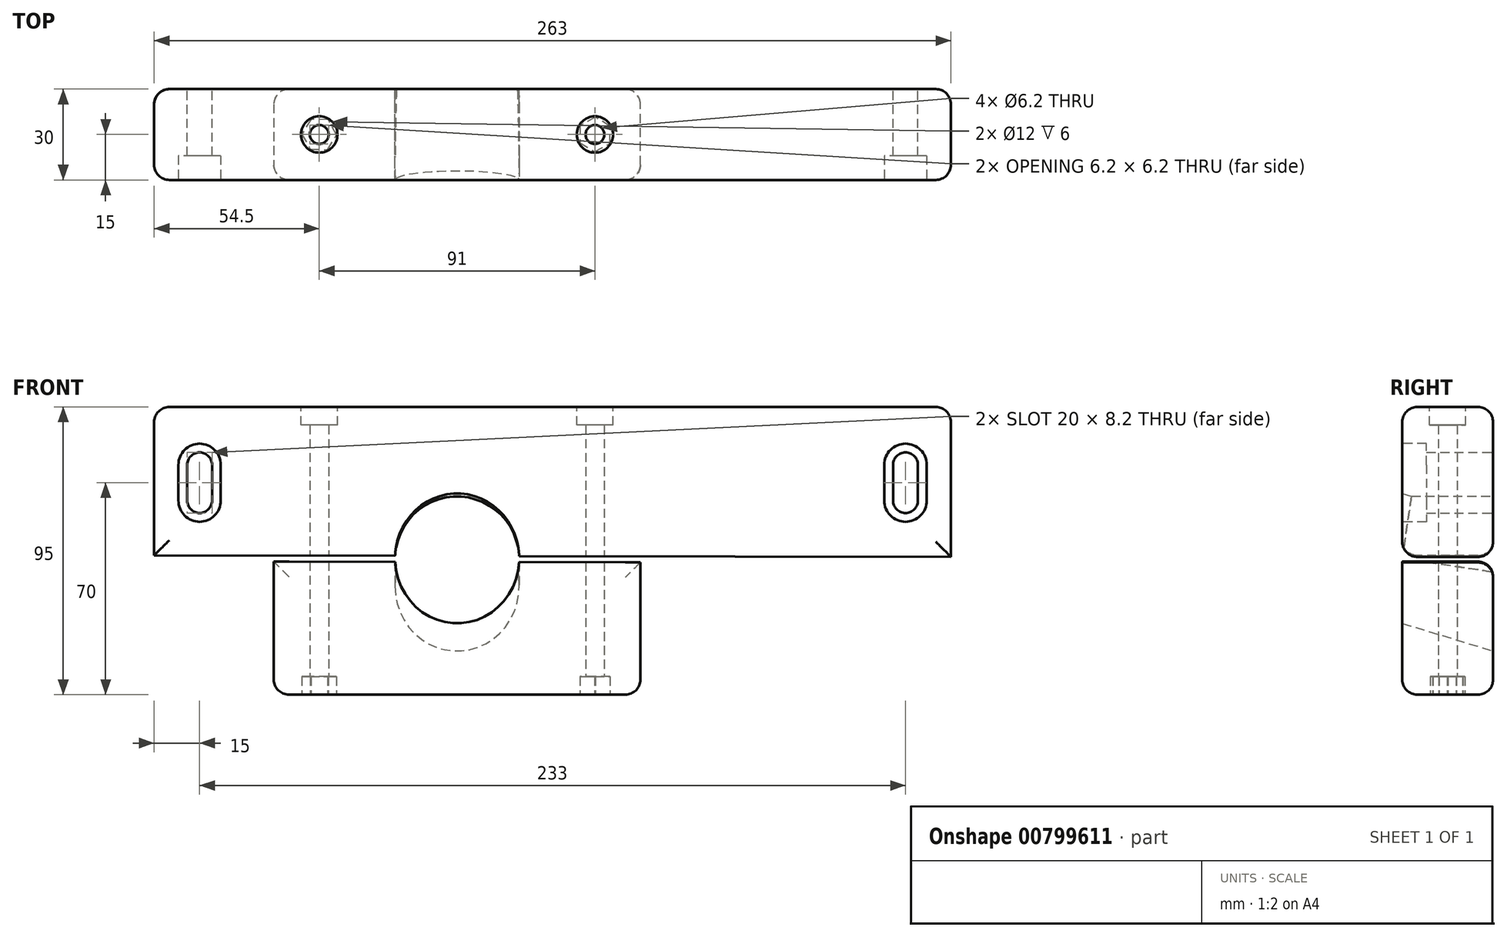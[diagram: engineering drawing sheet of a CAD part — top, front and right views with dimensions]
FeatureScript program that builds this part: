
annotation { "Feature Type Name" : "Feature", "Feature Type Description" : "" }
export const myFeature = defineFeature(function(context is Context, id is Id, definition is map)
    precondition{}
    {
        {
            var Q0;
            Q0=qCreatedBy(makeId("Front.planeOp"),FACE);
            var sketch = newSketch(context, id + "F0", { "sketchPlane" : qUnion([Q0])});
            skLineSegment(sketch, "E0", {"start": v(0, 0) * mm, "end": v(131.5, 0) * mm});
            skLineSegment(sketch, "E1", {"start": v(0, 0) * mm, "end": v(-131.5, 0) * mm});
            skLineSegment(sketch, "E2", {"start": v(-131.5, 0) * mm, "end": v(-131.5, -50) * mm});
            skLineSegment(sketch, "E3", {"start": v(131.5, 0) * mm, "end": v(131.5, -50) * mm});
            skLineSegment(sketch, "E4", {"start": v(131.5, -50) * mm, "end": v(-131.5, -50) * mm});
            skLineSegment(sketch, "E5.0", {"start": v(116.5, 0) * mm, "end": v(116.5, -19.1) * mm, "construction": true});
            skLineSegment(sketch, "E6.0", {"start": v(-116.5, 0) * mm, "end": v(-116.5, -19.1) * mm, "construction": true});
            skLineSegment(sketch, "E7.0", {"start": v(-112.4, 0) * mm, "end": v(-112.4, -50) * mm, "construction": true});
            skLineSegment(sketch, "E8.0", {"start": v(112.4, 0) * mm, "end": v(112.4, -50) * mm, "construction": true});
            skLineSegment(sketch, "E9.0", {"start": v(0, -19.1) * mm, "end": v(-131.5, -19.1) * mm, "construction": true});
            skLineSegment(sketch, "E10.0", {"start": v(131.5, -30.9) * mm, "end": v(-108.3, -30.9) * mm, "construction": true});
            skLineSegment(sketch, "E11.0", {"start": v(0, -19.1) * mm, "end": v(131.5, -19.1) * mm, "construction": true});
            skLineSegment(sketch, "E12.trimOffspring", {"start": v(-116.5, -30.9) * mm, "end": v(-131.5, -30.9) * mm, "construction": true});
            skArc(sketch, "E13", {"start": v(120.6, -19.1) * mm, "mid": v(116.5, -15) * mm, "end": v(112.4, -19.1) * mm});
            skArc(sketch, "E14", {"start": v(112.4, -30.9) * mm, "mid": v(116.5, -35) * mm, "end": v(120.6, -30.9) * mm});
            skArc(sketch, "E15", {"start": v(-120.6, -30.9) * mm, "mid": v(-116.5, -35) * mm, "end": v(-112.4, -30.9) * mm});
            skArc(sketch, "E16", {"start": v(-112.4, -19.1) * mm, "mid": v(-116.5, -15) * mm, "end": v(-120.6, -19.1) * mm});
            skLineSegment(sketch, "E17", {"start": v(-116.5, -25) * mm, "end": v(-31.5, -25) * mm, "construction": true});
            skLineSegment(sketch, "E18", {"start": v(-31.5, -25) * mm, "end": v(116.5, -25) * mm, "construction": true});
            skLineSegment(sketch, "E19.trimOffspring", {"start": v(116.5, -23.2) * mm, "end": v(116.5, -50) * mm, "construction": true});
            skLineSegment(sketch, "E20", {"start": v(120.6, -19.1) * mm, "end": v(120.6, -30.9) * mm});
            skLineSegment(sketch, "E21", {"start": v(112.4, -30.9) * mm, "end": v(112.4, -19.1) * mm});
            skLineSegment(sketch, "E22", {"start": v(-120.6, -19.1) * mm, "end": v(-120.6, -30.9) * mm});
            skLineSegment(sketch, "E23", {"start": v(-112.4, -19.1) * mm, "end": v(-112.4, -30.9) * mm});
            skLineSegment(sketch, "E24.trimOffspring", {"start": v(-116.5, -23.2) * mm, "end": v(-116.5, -50) * mm, "construction": true});
            skLineSegment(sketch, "E25", {"start": v(-31.5, -25) * mm, "end": v(-31.5, -50) * mm, "construction": true});
            skCircle(sketch, "E26", {"center": v(-31.5, -50) * mm, "radius": 20.5 * mm});
            skLineSegment(sketch, "E27", {"start": v(-52, -50) * mm, "end": v(-92, -50) * mm, "construction": true});
            skLineSegment(sketch, "E28", {"start": v(-92, -50) * mm, "end": v(-92, -95) * mm});
            skLineSegment(sketch, "E29", {"start": v(-92, -95) * mm, "end": v(29, -95) * mm});
            skLineSegment(sketch, "E30", {"start": v(29, -95) * mm, "end": v(29, -50) * mm});
            skSolve(sketch);
        }
        {
            var Q0;
            Q0=makeQuery(id+"F0.imprint","IMPRINT",FACE,{"disambiguationData":[TD([[makeQuery(id+"F0.imprint","IMPRINT",EDGE,{"derivedFrom":sQuery(id+"F0.wireOp",EDGE,"E0")}),-1.0]])]});
            var Q1;
            {var subQ0=sQuery(id+"F0.wireOp",EDGE,"E28");Q1=makeQuery(id+"F0.imprint","IMPRINT",FACE,{"disambiguationData":[TD([[makeQuery(id+"F0.imprint","IMPRINT",EDGE,{"derivedFrom":subQ0}),1.0]])]});}
            var Q2;
            {var subQ0=sQuery(id+"F0.wireOp",EDGE,"E26");var subQ1=sQuery(id+"F0.wireOp",EDGE,"E4");var subQ2=makeQuery(id+"F0.imprint","INTERSECT",VERTEX,{"disambiguationData":[OD(0.0)],"derivedFrom":[subQ1,subQ0]});Q2=makeQuery(id+"F0.imprint","IMPRINT",FACE,{"disambiguationData":[TD([[makeQuery(id+"F0.imprint","IMPRINT",EDGE,{"disambiguationData":[TD([[subQ2,-1.0]])],"derivedFrom":subQ1}),1.0]])]});}
            var Q3;
            {var subQ0=sQuery(id+"F0.wireOp",EDGE,"E26");var subQ1=sQuery(id+"F0.wireOp",EDGE,"E4");var subQ2=makeQuery(id+"F0.imprint","INTERSECT",VERTEX,{"disambiguationData":[OD(0.0)],"derivedFrom":[subQ1,subQ0]});Q3=makeQuery(id+"F0.imprint","IMPRINT",FACE,{"disambiguationData":[TD([[makeQuery(id+"F0.imprint","IMPRINT",EDGE,{"disambiguationData":[TD([[subQ2,-1.0]])],"derivedFrom":subQ1}),-1.0]])]});}
            extrude(context, id + "F1", {"entities" : qUnion([Q0, Q1, Q2, Q3]), "depth" : 30 * mm, "offsetDistance" : 25 * mm});
        }
        {
            var Q0;
            Q0=qCreatedBy(makeId("Front.planeOp"),FACE);
            var Q1;
            {var subQ0=sQuery(id+"F0.wireOp",EDGE,"E4");Q1=makeQuery(id+"F1.opExtrude","CAP_EDGE",EDGE,{"disambiguationData":[OSD([subQ0]),TDD([makeQuery(id+"F0.imprint","IMPRINT",EDGE,{"disambiguationData":[TD([[makeQuery(id+"F0.imprint","INTERSECT",VERTEX,{"derivedFrom":[sQuery(id+"F0.wireOp",EDGE,"E2"),subQ0]}),1.0]])],"derivedFrom":subQ0})])],"isStart":false});}
            cPlane(context, id + "F2", {"entities" : qUnion([Q0, Q1]), "cplaneType" : CPlaneType.LINE_ANGLE, "offset" : 25 * mm, "angle" : 17 * degree, "width" : 150 * mm, "height" : 150 * mm});
        }
        {
            var Q0;
            Q0=qCreatedBy(id+"F2.planeOp",FACE);
            var sketch = newSketch(context, id + "F3", { "sketchPlane" : qUnion([Q0])});
            skPoint(sketch, "E31", {"position": v(92, -56.59) * mm});
            skPoint(sketch, "E32", {"position": v(112.4, -56.59) * mm});
            skLineSegment(sketch, "E33", {"start": v(92, -56.59) * mm, "end": v(31.5, -56.59) * mm, "construction": true});
            skCircle(sketch, "E34", {"center": v(31.5, -56.59) * mm, "radius": 20.5 * mm});
            skSolve(sketch);
        }
        {
            var Q0;
            Q0=makeQuery(id+"F3.imprint","IMPRINT",FACE,{"disambiguationData":[TD([[makeQuery(id+"F3.imprint","IMPRINT",EDGE,{"derivedFrom":sQuery(id+"F3.wireOp",EDGE,"E34")}),1.0]])]});
            extrude(context, id + "F4", {"entities" : qUnion([Q0]), "operationType" : NewBodyOperationType.REMOVE, "endBound" : BoundingType.SYMMETRIC, "oppositeDirection" : true, "depth" : 80 * mm, "offsetDistance" : 25 * mm});
        }
        {
            var Q0;
            Q0=makeQuery(id+"F1.opExtrude","CAP_FACE",FACE,{"disambiguationData":[OSD([sQuery(id+"F0.wireOp",EDGE,"E0"),sQuery(id+"F0.wireOp",EDGE,"E1"),sQuery(id+"F0.wireOp",EDGE,"E2"),sQuery(id+"F0.wireOp",EDGE,"E3"),sQuery(id+"F0.wireOp",EDGE,"E4"),sQuery(id+"F0.wireOp",EDGE,"E13"),sQuery(id+"F0.wireOp",EDGE,"E14"),sQuery(id+"F0.wireOp",EDGE,"E15"),sQuery(id+"F0.wireOp",EDGE,"E16"),sQuery(id+"F0.wireOp",EDGE,"E20"),sQuery(id+"F0.wireOp",EDGE,"E21"),sQuery(id+"F0.wireOp",EDGE,"E22"),sQuery(id+"F0.wireOp",EDGE,"E23"),sQuery(id+"F0.wireOp",EDGE,"E28"),sQuery(id+"F0.wireOp",EDGE,"E29"),sQuery(id+"F0.wireOp",EDGE,"E30")])],"isStart":false});
            var sketch = newSketch(context, id + "F5", { "sketchPlane" : qUnion([Q0])});
            skLineSegment(sketch, "E35", {"start": v(-112.4, -19.1) * mm, "end": v(-120.6, -19.1) * mm, "construction": true});
            skLineSegment(sketch, "E36", {"start": v(-120.6, -19.1) * mm, "end": v(-120.6, -30.9) * mm, "construction": true});
            skArc(sketch, "E37", {"start": v(-109.5, -19.1) * mm, "mid": v(-116.5, -12.1) * mm, "end": v(-123.5, -19.1) * mm});
            skLineSegment(sketch, "E38", {"start": v(-123.5, -19.1) * mm, "end": v(-123.5, -30.9) * mm});
            skLineSegment(sketch, "E39", {"start": v(-109.5, -30.9) * mm, "end": v(-109.5, -19.1) * mm});
            skArc(sketch, "E40.trimOffspring", {"start": v(-123.5, -30.9) * mm, "mid": v(-116.5, -37.9) * mm, "end": v(-109.5, -30.9) * mm});
            skPoint(sketch, "E41.end.orphan", {"position": v(-112.4, -30.9) * mm});
            skLineSegment(sketch, "E42.MirrorCS", {"start": v(109.5, -30.9) * mm, "end": v(109.5, -19.1) * mm});
            skLineSegment(sketch, "E43.MirrorCS", {"start": v(123.5, -19.1) * mm, "end": v(123.5, -30.9) * mm});
            skArc(sketch, "E44.MirrorCS", {"start": v(109.5, -19.1) * mm, "mid": v(116.5, -12.1) * mm, "end": v(123.5, -19.1) * mm});
            skArc(sketch, "E45.MirrorCS", {"start": v(123.5, -30.9) * mm, "mid": v(116.5, -37.9) * mm, "end": v(109.5, -30.9) * mm});
            skSolve(sketch);
        }
        {
            var Q0;
            Q0=makeQuery(id+"F5.imprint","IMPRINT",FACE,{"disambiguationData":[TD([[makeQuery(id+"F5.imprint","IMPRINT",EDGE,{"derivedFrom":sQuery(id+"F5.wireOp",EDGE,"E37")}),1.0]])]});
            var Q1;
            Q1=makeQuery(id+"F5.imprint","IMPRINT",FACE,{"disambiguationData":[TD([[makeQuery(id+"F5.imprint","IMPRINT",EDGE,{"derivedFrom":sQuery(id+"F5.wireOp",EDGE,"E42.MirrorCS")}),-1.0]])]});
            extrude(context, id + "F6", {"entities" : qUnion([Q0, Q1]), "operationType" : NewBodyOperationType.REMOVE, "oppositeDirection" : true, "depth" : 8 * mm, "offsetDistance" : 25 * mm});
        }
        {
            var Q0;
            Q0=makeQuery(id+"F1.opExtrude","SWEPT_FACE",FACE,{"disambiguationData":[OSD([sQuery(id+"F0.wireOp",EDGE,"E29")])]});
            var sketch = newSketch(context, id + "F7", { "sketchPlane" : qUnion([Q0])});
            skLineSegment(sketch, "E46", {"start": v(-92, 30) * mm, "end": v(-92, 0) * mm, "construction": true});
            skLineSegment(sketch, "E47", {"start": v(-92, 0) * mm, "end": v(29, 0) * mm, "construction": true});
            skLineSegment(sketch, "E48", {"start": v(29, 0) * mm, "end": v(29, 15) * mm, "construction": true});
            skLineSegment(sketch, "E49", {"start": v(29, 15) * mm, "end": v(-92, 15) * mm, "construction": true});
            skLineSegment(sketch, "E50", {"start": v(-92, 15) * mm, "end": v(-77, 15) * mm, "construction": true});
            skLineSegment(sketch, "E51", {"start": v(-77, 15) * mm, "end": v(14, 15) * mm, "construction": true});
            skCircle(sketch, "E52", {"center": v(-77, 15) * mm, "radius": 3.1 * mm});
            skCircle(sketch, "E53", {"center": v(14, 15) * mm, "radius": 3.1 * mm});
            skCircle(sketch, "E54.cCircle", {"center": v(-77, 15) * mm, "radius": 4.95 * mm, "construction": true});
            skLineSegment(sketch, "E54.0", {"start": v(-74.24, 20) * mm, "end": v(-71.29, 15.1) * mm});
            skLineSegment(sketch, "E54.1", {"start": v(-71.29, 15.1) * mm, "end": v(-74.05, 10.1) * mm});
            skLineSegment(sketch, "E54.2", {"start": v(-74.05, 10.1) * mm, "end": v(-79.76, 10) * mm});
            skLineSegment(sketch, "E54.3", {"start": v(-79.76, 10) * mm, "end": v(-82.71, 14.9) * mm});
            skLineSegment(sketch, "E54.4", {"start": v(-82.71, 14.9) * mm, "end": v(-79.95, 19.9) * mm});
            skLineSegment(sketch, "E54.5", {"start": v(-79.95, 19.9) * mm, "end": v(-74.24, 20) * mm});
            skPoint(sketch, "E54.0.midPoint", {"position": v(-72.76, 17.56) * mm});
            skCircle(sketch, "E55.cCircle", {"center": v(14, 15) * mm, "radius": 4.95 * mm, "construction": true});
            skLineSegment(sketch, "E55.0", {"start": v(9, 17.76) * mm, "end": v(13.9, 20.71) * mm});
            skLineSegment(sketch, "E55.1", {"start": v(13.9, 20.71) * mm, "end": v(18.9, 17.95) * mm});
            skLineSegment(sketch, "E55.2", {"start": v(18.9, 17.95) * mm, "end": v(19, 12.24) * mm});
            skLineSegment(sketch, "E55.3", {"start": v(19, 12.24) * mm, "end": v(14.1, 9.29) * mm});
            skLineSegment(sketch, "E55.4", {"start": v(14.1, 9.29) * mm, "end": v(9.1, 12.05) * mm});
            skLineSegment(sketch, "E55.5", {"start": v(9.1, 12.05) * mm, "end": v(9, 17.76) * mm});
            skPoint(sketch, "E55.0.midPoint", {"position": v(11.44, 19.24) * mm});
            skSolve(sketch);
        }
        {
            var Q0;
            Q0=makeQuery(id+"F7.imprint","IMPRINT",FACE,{"disambiguationData":[TD([[makeQuery(id+"F7.imprint","IMPRINT",EDGE,{"derivedFrom":sQuery(id+"F7.wireOp",EDGE,"E52")}),1.0]])]});
            var Q1;
            Q1=makeQuery(id+"F7.imprint","IMPRINT",FACE,{"disambiguationData":[TD([[makeQuery(id+"F7.imprint","IMPRINT",EDGE,{"derivedFrom":sQuery(id+"F7.wireOp",EDGE,"E53")}),1.0]])]});
            extrude(context, id + "F8", {"entities" : qUnion([Q0, Q1]), "operationType" : NewBodyOperationType.REMOVE, "endBound" : BoundingType.UP_TO_NEXT, "oppositeDirection" : true, "depth" : 25 * mm, "offsetDistance" : 25 * mm});
        }
        {
            var Q0;
            Q0=makeQuery(id+"F7.imprint","IMPRINT",FACE,{"disambiguationData":[TD([[makeQuery(id+"F7.imprint","IMPRINT",EDGE,{"derivedFrom":sQuery(id+"F7.wireOp",EDGE,"E52")}),-1.0]])]});
            var Q1;
            Q1=makeQuery(id+"F7.imprint","IMPRINT",FACE,{"disambiguationData":[TD([[makeQuery(id+"F7.imprint","IMPRINT",EDGE,{"derivedFrom":sQuery(id+"F7.wireOp",EDGE,"E53")}),-1.0]])]});
            extrude(context, id + "F9", {"entities" : qUnion([Q0, Q1]), "operationType" : NewBodyOperationType.REMOVE, "oppositeDirection" : true, "depth" : 6 * mm, "offsetDistance" : 25 * mm});
        }
        {
            var Q0;
            Q0=makeQuery(id+"F1.opExtrude","SWEPT_FACE",FACE,{"disambiguationData":[OSD([sQuery(id+"F0.wireOp",EDGE,"E0"),sQuery(id+"F0.wireOp",EDGE,"E1")])]});
            var sketch = newSketch(context, id + "F10", { "sketchPlane" : qUnion([Q0])});
            skCircle(sketch, "E56", {"center": v(-77, -15) * mm, "radius": 6 * mm});
            skCircle(sketch, "E57", {"center": v(14, -15) * mm, "radius": 6 * mm});
            skSolve(sketch);
        }
        {
            var Q0;
            Q0 = qSketchRegion(id + "F10", true);
            extrude(context, id + "F11", {"entities" : qUnion([Q0]), "operationType" : NewBodyOperationType.REMOVE, "oppositeDirection" : true, "depth" : 6 * mm, "offsetDistance" : 25 * mm});
        }
        {
            var Q0;
            Q0=makeQuery(id+"F1.opExtrude","CAP_FACE",FACE,{"disambiguationData":[OSD([sQuery(id+"F0.wireOp",EDGE,"E0"),sQuery(id+"F0.wireOp",EDGE,"E1"),sQuery(id+"F0.wireOp",EDGE,"E2"),sQuery(id+"F0.wireOp",EDGE,"E3"),sQuery(id+"F0.wireOp",EDGE,"E4"),sQuery(id+"F0.wireOp",EDGE,"E13"),sQuery(id+"F0.wireOp",EDGE,"E14"),sQuery(id+"F0.wireOp",EDGE,"E15"),sQuery(id+"F0.wireOp",EDGE,"E16"),sQuery(id+"F0.wireOp",EDGE,"E20"),sQuery(id+"F0.wireOp",EDGE,"E21"),sQuery(id+"F0.wireOp",EDGE,"E22"),sQuery(id+"F0.wireOp",EDGE,"E23"),sQuery(id+"F0.wireOp",EDGE,"E28"),sQuery(id+"F0.wireOp",EDGE,"E29"),sQuery(id+"F0.wireOp",EDGE,"E30")])],"isStart":false});
            var sketch = newSketch(context, id + "F12", { "sketchPlane" : qUnion([Q0])});
            skLineSegment(sketch, "E58", {"start": v(-131.5, -50) * mm, "end": v(-131.5, -49) * mm});
            skLineSegment(sketch, "E59", {"start": v(-131.5, -49) * mm, "end": v(131.5, -49.5) * mm});
            skPoint(sketch, "E59.endSnap0", {"position": v(-131.5, -49.5) * mm});
            skLineSegment(sketch, "E60", {"start": v(131.5, -49.5) * mm, "end": v(131.5, -51.5) * mm});
            skLineSegment(sketch, "E61", {"start": v(-131.5, -49) * mm, "end": v(-131.5, -51) * mm});
            skLineSegment(sketch, "E62", {"start": v(-131.5, -51) * mm, "end": v(131.5, -51.5) * mm});
            skSolve(sketch);
        }
        {
            var Q0;
            {var subQ4=sQuery(id+"F0.wireOp",EDGE,"E4");var subQ5=sQuery(id+"F0.wireOp",EDGE,"E2");var subQ8=makeQuery(id+"F1.opExtrude","CAP_EDGE",EDGE,{"disambiguationData":[OSD([subQ4]),TDD([makeQuery(id+"F0.imprint","IMPRINT",EDGE,{"disambiguationData":[TD([[makeQuery(id+"F0.imprint","INTERSECT",VERTEX,{"derivedFrom":[subQ5,subQ4]}),1.0]])],"derivedFrom":subQ4})])],"isStart":false});Q0=makeQuery(id+"F12.imprint","IMPRINT",FACE,{"disambiguationData":[TD([[makeQuery(id+"F12.imprint","IMPRINT",EDGE,{"derivedFrom":subQ8}),-1.0]])]});}
            var Q1;
            {var subQ0=sQuery(id+"F12.wireOp",EDGE,"E59");var subQ1=makeQuery(id+"F4.boolean.opBoolean","INTERSECT",EDGE,{"derivedFrom":[makeQuery(id+"F1.opExtrude","CAP_FACE",FACE,{"disambiguationData":[OSD([sQuery(id+"F0.wireOp",EDGE,"E0"),sQuery(id+"F0.wireOp",EDGE,"E1"),sQuery(id+"F0.wireOp",EDGE,"E2"),sQuery(id+"F0.wireOp",EDGE,"E3"),sQuery(id+"F0.wireOp",EDGE,"E4"),sQuery(id+"F0.wireOp",EDGE,"E13"),sQuery(id+"F0.wireOp",EDGE,"E14"),sQuery(id+"F0.wireOp",EDGE,"E15"),sQuery(id+"F0.wireOp",EDGE,"E16"),sQuery(id+"F0.wireOp",EDGE,"E20"),sQuery(id+"F0.wireOp",EDGE,"E21"),sQuery(id+"F0.wireOp",EDGE,"E22"),sQuery(id+"F0.wireOp",EDGE,"E23"),sQuery(id+"F0.wireOp",EDGE,"E28"),sQuery(id+"F0.wireOp",EDGE,"E29"),sQuery(id+"F0.wireOp",EDGE,"E30")])],"isStart":false}),makeQuery(id+"F4.opExtrude","SWEPT_FACE",FACE,{"disambiguationData":[OSD([sQuery(id+"F3.wireOp",EDGE,"E34")])]})]});var subQ2=makeQuery(id+"F12.imprint","INTERSECT",VERTEX,{"disambiguationData":[OD(0.0)],"derivedFrom":[subQ1,subQ0]});Q1=makeQuery(id+"F12.imprint","IMPRINT",FACE,{"disambiguationData":[TD([[makeQuery(id+"F12.imprint","IMPRINT",EDGE,{"disambiguationData":[TD([[subQ2,-1.0]])],"derivedFrom":subQ0}),-1.0]])]});}
            var Q2;
            {var subQ0=sQuery(id+"F0.wireOp",EDGE,"E4");var subQ1=sQuery(id+"F0.wireOp",EDGE,"E3");var subQ3=makeQuery(id+"F1.opExtrude","CAP_EDGE",EDGE,{"disambiguationData":[OSD([subQ0]),TDD([makeQuery(id+"F0.imprint","IMPRINT",EDGE,{"disambiguationData":[TD([[makeQuery(id+"F0.imprint","INTERSECT",VERTEX,{"derivedFrom":[subQ1,subQ0]}),-1.0]])],"derivedFrom":subQ0})])],"isStart":false});Q2=makeQuery(id+"F12.imprint","IMPRINT",FACE,{"disambiguationData":[TD([[makeQuery(id+"F12.imprint","IMPRINT",EDGE,{"derivedFrom":subQ3}),-1.0]])]});}
            extrude(context, id + "F13", {"entities" : qUnion([Q0, Q1, Q2]), "operationType" : NewBodyOperationType.REMOVE, "oppositeDirection" : true, "depth" : 50 * mm, "offsetDistance" : 25 * mm});
        }
        {
            var Q0;
            Q0=makeQuery(id+"F1.opExtrude","CAP_EDGE",EDGE,{"disambiguationData":[OSD([sQuery(id+"F0.wireOp",EDGE,"E0"),sQuery(id+"F0.wireOp",EDGE,"E1")])],"isStart":false});
            var Q1;
            Q1=makeQuery(id+"F1.opExtrude","CAP_EDGE",EDGE,{"disambiguationData":[OSD([sQuery(id+"F0.wireOp",EDGE,"E2")])],"isStart":false});
            var Q2;
            Q2=makeQuery(id+"F1.opExtrude","CAP_EDGE",EDGE,{"disambiguationData":[OSD([sQuery(id+"F0.wireOp",EDGE,"E3")])],"isStart":false});
            var Q3;
            {var subQ0=sQuery(id+"F0.wireOp",EDGE,"E3");var subQ1=sQuery(id+"F12.wireOp",EDGE,"E59");Q3=makeQuery(id+"F13.boolean.opBoolean","COPY",EDGE,{"disambiguationData":[TD([makeQuery(id+"F1.opExtrude","SWEPT_FACE",FACE,{"disambiguationData":[OSD([subQ0])]})])],"derivedFrom":makeQuery(id+"F13.opExtrude","CAP_EDGE",EDGE,{"disambiguationData":[OSD([subQ1])],"isStart":true})});}
            var Q4;
            {var subQ0=sQuery(id+"F0.wireOp",EDGE,"E2");var subQ1=sQuery(id+"F12.wireOp",EDGE,"E59");Q4=makeQuery(id+"F13.boolean.opBoolean","COPY",EDGE,{"disambiguationData":[TD([makeQuery(id+"F1.opExtrude","SWEPT_FACE",FACE,{"disambiguationData":[OSD([subQ0])]})])],"derivedFrom":makeQuery(id+"F13.opExtrude","CAP_EDGE",EDGE,{"disambiguationData":[OSD([subQ1])],"isStart":true})});}
            var Q5;
            Q5=makeQuery(id+"F1.opExtrude","CAP_EDGE",EDGE,{"disambiguationData":[OSD([sQuery(id+"F0.wireOp",EDGE,"E29")])],"isStart":false});
            var Q6;
            Q6=makeQuery(id+"F1.opExtrude","CAP_EDGE",EDGE,{"disambiguationData":[OSD([sQuery(id+"F0.wireOp",EDGE,"E28")])],"isStart":false});
            var Q7;
            {var subQ0=sQuery(id+"F0.wireOp",EDGE,"E28");var subQ1=sQuery(id+"F12.wireOp",EDGE,"E62");Q7=makeQuery(id+"F13.boolean.opBoolean","COPY",EDGE,{"disambiguationData":[TD([makeQuery(id+"F1.opExtrude","SWEPT_FACE",FACE,{"disambiguationData":[OSD([subQ0])]})])],"derivedFrom":makeQuery(id+"F13.opExtrude","CAP_EDGE",EDGE,{"disambiguationData":[OSD([subQ1])],"isStart":true})});}
            var Q8;
            {var subQ0=sQuery(id+"F0.wireOp",EDGE,"E30");var subQ1=sQuery(id+"F12.wireOp",EDGE,"E62");Q8=makeQuery(id+"F13.boolean.opBoolean","COPY",EDGE,{"disambiguationData":[TD([makeQuery(id+"F1.opExtrude","SWEPT_FACE",FACE,{"disambiguationData":[OSD([subQ0])]})])],"derivedFrom":makeQuery(id+"F13.opExtrude","CAP_EDGE",EDGE,{"disambiguationData":[OSD([subQ1])],"isStart":true})});}
            var Q9;
            Q9=makeQuery(id+"F1.opExtrude","CAP_EDGE",EDGE,{"disambiguationData":[OSD([sQuery(id+"F0.wireOp",EDGE,"E30")])],"isStart":false});
            var Q10;
            Q10=makeQuery(id+"F1.opExtrude","SWEPT_EDGE",EDGE,{"disambiguationData":[OSD([sQuery(id+"F0.wireOp",EDGE,"E29"),sQuery(id+"F0.wireOp",EDGE,"E30")])]});
            var Q11;
            Q11=makeQuery(id+"F1.opExtrude","CAP_EDGE",EDGE,{"disambiguationData":[OSD([sQuery(id+"F0.wireOp",EDGE,"E30")])],"isStart":true});
            var Q12;
            Q12=makeQuery(id+"F1.opExtrude","CAP_EDGE",EDGE,{"disambiguationData":[OSD([sQuery(id+"F0.wireOp",EDGE,"E29")])],"isStart":true});
            var Q13;
            Q13=makeQuery(id+"F13.boolean.opBoolean","INTERSECT",EDGE,{"disambiguationData":[OD(1.0)],"derivedFrom":[makeQuery(id+"F1.opExtrude","CAP_FACE",FACE,{"disambiguationData":[OSD([sQuery(id+"F0.wireOp",EDGE,"E0"),sQuery(id+"F0.wireOp",EDGE,"E1"),sQuery(id+"F0.wireOp",EDGE,"E2"),sQuery(id+"F0.wireOp",EDGE,"E3"),sQuery(id+"F0.wireOp",EDGE,"E4"),sQuery(id+"F0.wireOp",EDGE,"E13"),sQuery(id+"F0.wireOp",EDGE,"E14"),sQuery(id+"F0.wireOp",EDGE,"E15"),sQuery(id+"F0.wireOp",EDGE,"E16"),sQuery(id+"F0.wireOp",EDGE,"E20"),sQuery(id+"F0.wireOp",EDGE,"E21"),sQuery(id+"F0.wireOp",EDGE,"E22"),sQuery(id+"F0.wireOp",EDGE,"E23"),sQuery(id+"F0.wireOp",EDGE,"E28"),sQuery(id+"F0.wireOp",EDGE,"E29"),sQuery(id+"F0.wireOp",EDGE,"E30")])],"isStart":true}),makeQuery(id+"F13.opExtrude","SWEPT_FACE",FACE,{"disambiguationData":[OSD([sQuery(id+"F12.wireOp",EDGE,"E62")])]})]});
            var Q14;
            Q14=makeQuery(id+"F1.opExtrude","CAP_EDGE",EDGE,{"disambiguationData":[OSD([sQuery(id+"F0.wireOp",EDGE,"E28")])],"isStart":true});
            var Q15;
            Q15=makeQuery(id+"F13.boolean.opBoolean","INTERSECT",EDGE,{"disambiguationData":[OD(0.0)],"derivedFrom":[makeQuery(id+"F1.opExtrude","CAP_FACE",FACE,{"disambiguationData":[OSD([sQuery(id+"F0.wireOp",EDGE,"E0"),sQuery(id+"F0.wireOp",EDGE,"E1"),sQuery(id+"F0.wireOp",EDGE,"E2"),sQuery(id+"F0.wireOp",EDGE,"E3"),sQuery(id+"F0.wireOp",EDGE,"E4"),sQuery(id+"F0.wireOp",EDGE,"E13"),sQuery(id+"F0.wireOp",EDGE,"E14"),sQuery(id+"F0.wireOp",EDGE,"E15"),sQuery(id+"F0.wireOp",EDGE,"E16"),sQuery(id+"F0.wireOp",EDGE,"E20"),sQuery(id+"F0.wireOp",EDGE,"E21"),sQuery(id+"F0.wireOp",EDGE,"E22"),sQuery(id+"F0.wireOp",EDGE,"E23"),sQuery(id+"F0.wireOp",EDGE,"E28"),sQuery(id+"F0.wireOp",EDGE,"E29"),sQuery(id+"F0.wireOp",EDGE,"E30")])],"isStart":true}),makeQuery(id+"F13.opExtrude","SWEPT_FACE",FACE,{"disambiguationData":[OSD([sQuery(id+"F12.wireOp",EDGE,"E62")])]})]});
            var Q16;
            Q16=makeQuery(id+"F1.opExtrude","SWEPT_EDGE",EDGE,{"disambiguationData":[OSD([sQuery(id+"F0.wireOp",EDGE,"E28"),sQuery(id+"F0.wireOp",EDGE,"E29")])]});
            var Q17;
            Q17=makeQuery(id+"F1.opExtrude","CAP_EDGE",EDGE,{"disambiguationData":[OSD([sQuery(id+"F0.wireOp",EDGE,"E2")])],"isStart":true});
            var Q18;
            Q18=makeQuery(id+"F1.opExtrude","CAP_EDGE",EDGE,{"disambiguationData":[OSD([sQuery(id+"F0.wireOp",EDGE,"E0"),sQuery(id+"F0.wireOp",EDGE,"E1")])],"isStart":true});
            var Q19;
            Q19=makeQuery(id+"F13.boolean.opBoolean","INTERSECT",EDGE,{"disambiguationData":[OD(0.0)],"derivedFrom":[makeQuery(id+"F1.opExtrude","CAP_FACE",FACE,{"disambiguationData":[OSD([sQuery(id+"F0.wireOp",EDGE,"E0"),sQuery(id+"F0.wireOp",EDGE,"E1"),sQuery(id+"F0.wireOp",EDGE,"E2"),sQuery(id+"F0.wireOp",EDGE,"E3"),sQuery(id+"F0.wireOp",EDGE,"E4"),sQuery(id+"F0.wireOp",EDGE,"E13"),sQuery(id+"F0.wireOp",EDGE,"E14"),sQuery(id+"F0.wireOp",EDGE,"E15"),sQuery(id+"F0.wireOp",EDGE,"E16"),sQuery(id+"F0.wireOp",EDGE,"E20"),sQuery(id+"F0.wireOp",EDGE,"E21"),sQuery(id+"F0.wireOp",EDGE,"E22"),sQuery(id+"F0.wireOp",EDGE,"E23"),sQuery(id+"F0.wireOp",EDGE,"E28"),sQuery(id+"F0.wireOp",EDGE,"E29"),sQuery(id+"F0.wireOp",EDGE,"E30")])],"isStart":true}),makeQuery(id+"F13.opExtrude","SWEPT_FACE",FACE,{"disambiguationData":[OSD([sQuery(id+"F12.wireOp",EDGE,"E59")])]})]});
            var Q20;
            Q20=makeQuery(id+"F13.boolean.opBoolean","INTERSECT",EDGE,{"disambiguationData":[OD(1.0)],"derivedFrom":[makeQuery(id+"F1.opExtrude","CAP_FACE",FACE,{"disambiguationData":[OSD([sQuery(id+"F0.wireOp",EDGE,"E0"),sQuery(id+"F0.wireOp",EDGE,"E1"),sQuery(id+"F0.wireOp",EDGE,"E2"),sQuery(id+"F0.wireOp",EDGE,"E3"),sQuery(id+"F0.wireOp",EDGE,"E4"),sQuery(id+"F0.wireOp",EDGE,"E13"),sQuery(id+"F0.wireOp",EDGE,"E14"),sQuery(id+"F0.wireOp",EDGE,"E15"),sQuery(id+"F0.wireOp",EDGE,"E16"),sQuery(id+"F0.wireOp",EDGE,"E20"),sQuery(id+"F0.wireOp",EDGE,"E21"),sQuery(id+"F0.wireOp",EDGE,"E22"),sQuery(id+"F0.wireOp",EDGE,"E23"),sQuery(id+"F0.wireOp",EDGE,"E28"),sQuery(id+"F0.wireOp",EDGE,"E29"),sQuery(id+"F0.wireOp",EDGE,"E30")])],"isStart":true}),makeQuery(id+"F13.opExtrude","SWEPT_FACE",FACE,{"disambiguationData":[OSD([sQuery(id+"F12.wireOp",EDGE,"E59")])]})]});
            var Q21;
            Q21=makeQuery(id+"F1.opExtrude","CAP_EDGE",EDGE,{"disambiguationData":[OSD([sQuery(id+"F0.wireOp",EDGE,"E3")])],"isStart":true});
            var Q22;
            Q22=makeQuery(id+"F13.boolean.opBoolean","COPY",EDGE,{"derivedFrom":makeQuery(id+"F13.opExtrude","SWEPT_EDGE",EDGE,{"disambiguationData":[OSD([sQuery(id+"F0.wireOp",EDGE,"E3"),sQuery(id+"F12.wireOp",EDGE,"E59"),sQuery(id+"F12.wireOp",EDGE,"E60")])]})});
            var Q23;
            Q23=makeQuery(id+"F1.opExtrude","SWEPT_EDGE",EDGE,{"disambiguationData":[OSD([sQuery(id+"F0.wireOp",EDGE,"E0"),sQuery(id+"F0.wireOp",EDGE,"E3")])]});
            var Q24;
            Q24=makeQuery(id+"F1.opExtrude","SWEPT_EDGE",EDGE,{"disambiguationData":[OSD([sQuery(id+"F0.wireOp",EDGE,"E1"),sQuery(id+"F0.wireOp",EDGE,"E2")])]});
            fillet(context, id + "F14", {"entities" : qUnion([Q0, Q1, Q2, Q3, Q4, Q5, Q6, Q7, Q8, Q9, Q10, Q11, Q12, Q13, Q14, Q15, Q16, Q17, Q18, Q19, Q20, Q21, Q22, Q23, Q24]), "radius" : 5 * mm, "tangentPropagation" : true, "allowEdgeOverflow" : false});
        }
    });
